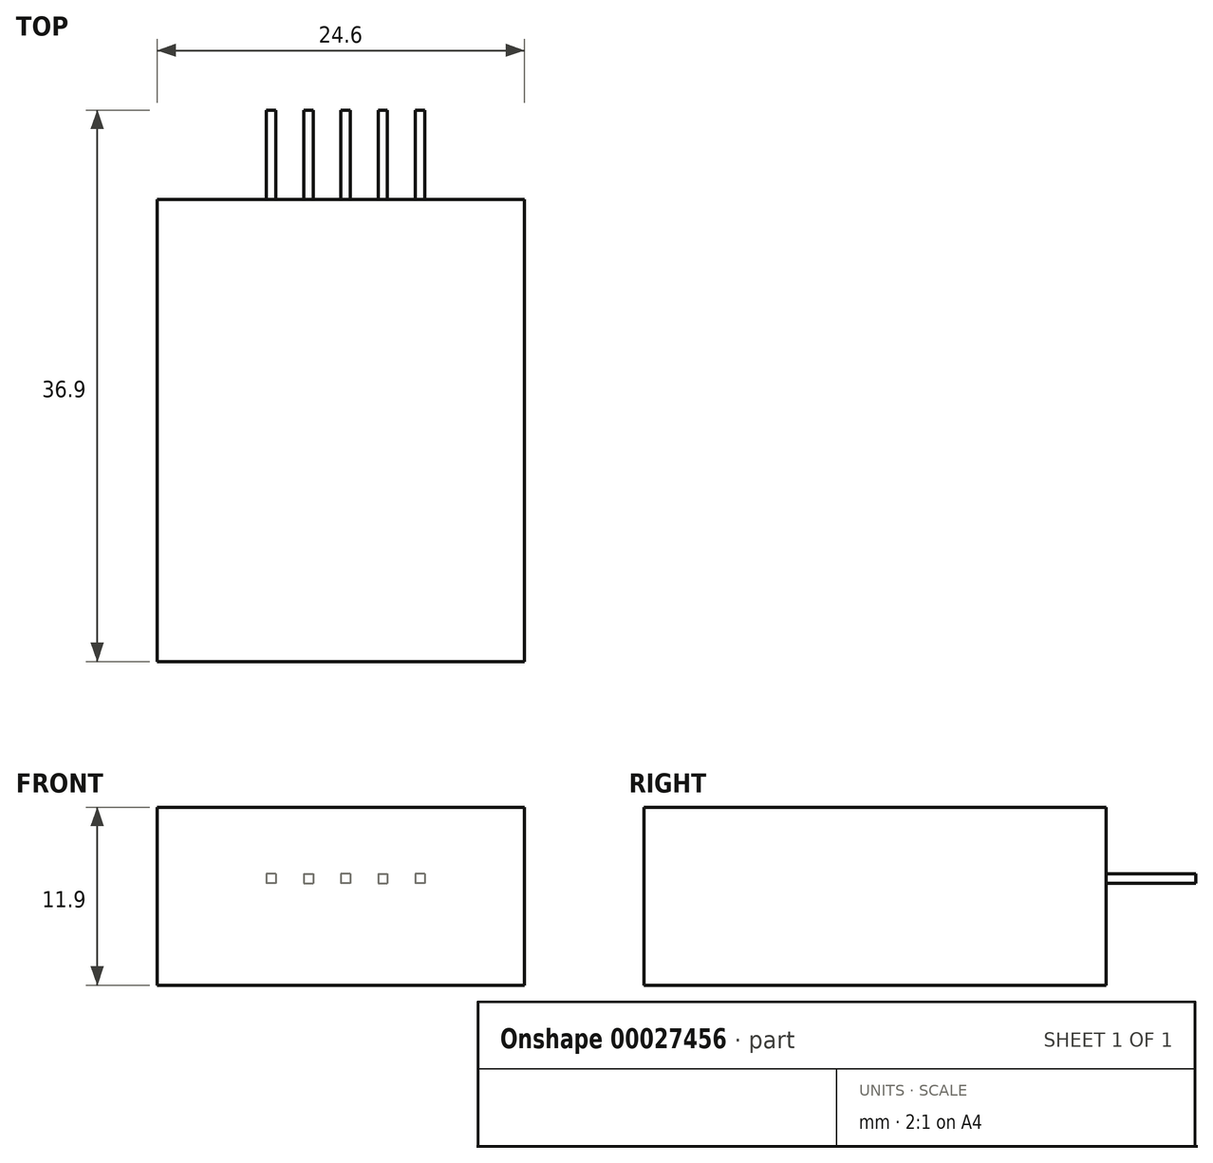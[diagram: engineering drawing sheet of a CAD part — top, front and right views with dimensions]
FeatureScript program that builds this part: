
annotation { "Feature Type Name" : "Feature", "Feature Type Description" : "" }
export const myFeature = defineFeature(function(context is Context, id is Id, definition is map)
    precondition{}
    {
        {
            var Q0;
            Q0=qCreatedBy(makeId("Top.planeOp"),FACE);
            var sketch = newSketch(context, id + "F0", { "sketchPlane" : qUnion([Q0])});
            skLineSegment(sketch, "E0.rect.bottom", {"start": v(12.3, 15.45) * mm, "end": v(-12.3, 15.45) * mm});
            skLineSegment(sketch, "E0.rect.top", {"start": v(12.3, -15.45) * mm, "end": v(-12.3, -15.45) * mm});
            skLineSegment(sketch, "E0.rect.left", {"start": v(12.3, 15.45) * mm, "end": v(12.3, -15.45) * mm});
            skLineSegment(sketch, "E0.rect.right", {"start": v(-12.3, 15.45) * mm, "end": v(-12.3, -15.45) * mm});
            skPoint(sketch, "E0.rect.middle", {"position": v(0, 0) * mm});
            skSolve(sketch);
        }
        {
            var Q0;
            Q0=makeQuery(id+"F0.imprint","IMPRINT",FACE,{"disambiguationData":[TD([[makeQuery(id+"F0.imprint","IMPRINT",EDGE,{"derivedFrom":sQuery(id+"F0.wireOp",EDGE,"E0.rect.bottom")}),1.0]])]});
            extrude(context, id + "F1", {"entities" : qUnion([Q0]), "depth" : 11.9 * mm});
        }
        {
            var Q0;
            Q0=makeQuery(id+"F1.opExtrude","SWEPT_FACE",FACE,{"disambiguationData":[OSD([sQuery(id+"F0.wireOp",EDGE,"E0.rect.bottom")])]});
            var sketch = newSketch(context, id + "F2", { "sketchPlane" : qUnion([Q0])});
            skLineSegment(sketch, "E1.bottom", {"start": v(-6.55, 8.44) * mm, "end": v(5.9, 8.44) * mm});
            skLineSegment(sketch, "E1.top", {"start": v(-6.55, 5.84) * mm, "end": v(5.9, 5.84) * mm});
            skLineSegment(sketch, "E1.left", {"start": v(-6.55, 8.44) * mm, "end": v(-6.55, 5.84) * mm});
            skLineSegment(sketch, "E1.right", {"start": v(5.9, 8.44) * mm, "end": v(5.9, 5.84) * mm});
            skLineSegment(sketch, "E2", {"start": v(-4.06, 8.44) * mm, "end": v(-4.06, 5.84) * mm});
            skLineSegment(sketch, "E3", {"start": v(-1.57, 8.44) * mm, "end": v(-1.57, 5.84) * mm});
            skLineSegment(sketch, "E4", {"start": v(0.92, 8.44) * mm, "end": v(0.92, 5.84) * mm});
            skLineSegment(sketch, "E5", {"start": v(3.4, 8.44) * mm, "end": v(3.4, 5.84) * mm});
            skLineSegment(sketch, "E6.bottom", {"start": v(-5.62, 7.45) * mm, "end": v(-5, 7.45) * mm});
            skLineSegment(sketch, "E6.top", {"start": v(-5.62, 6.82) * mm, "end": v(-5, 6.82) * mm});
            skLineSegment(sketch, "E6.left", {"start": v(-5.62, 7.45) * mm, "end": v(-5.62, 6.82) * mm});
            skLineSegment(sketch, "E6.right", {"start": v(-5, 7.46) * mm, "end": v(-5, 6.82) * mm});
            skLineSegment(sketch, "E7", {"start": v(-5.3, 8.44) * mm, "end": v(-5.3, 7.45) * mm, "construction": true});
            skLineSegment(sketch, "E8", {"start": v(-5, 7.14) * mm, "end": v(-4.06, 7.14) * mm, "construction": true});
            skLineSegment(sketch, "E9", {"start": v(-5.3, 6.82) * mm, "end": v(-5.3, 5.84) * mm, "construction": true});
            skLineSegment(sketch, "E10", {"start": v(-6.55, 7.14) * mm, "end": v(-5.62, 7.14) * mm, "construction": true});
            skLineSegment(sketch, "E11.MirrorCS", {"start": v(-3.13, 7.46) * mm, "end": v(-3.13, 6.82) * mm});
            skLineSegment(sketch, "E12.MirrorCS", {"start": v(-2.5, 7.45) * mm, "end": v(-3.13, 7.45) * mm});
            skLineSegment(sketch, "E13.MirrorCS", {"start": v(-2.5, 7.45) * mm, "end": v(-2.5, 6.82) * mm});
            skLineSegment(sketch, "E14.MirrorCS", {"start": v(-2.5, 6.82) * mm, "end": v(-3.13, 6.82) * mm});
            skLineSegment(sketch, "E15.MirrorCS", {"start": v(-0.64, 7.46) * mm, "end": v(-0.01, 7.46) * mm});
            skLineSegment(sketch, "E16.MirrorCS", {"start": v(-0.64, 7.46) * mm, "end": v(-0.64, 6.82) * mm});
            skLineSegment(sketch, "E17.MirrorCS", {"start": v(-0.01, 7.46) * mm, "end": v(-0.01, 6.82) * mm});
            skLineSegment(sketch, "E18.MirrorCS", {"start": v(-0.64, 6.82) * mm, "end": v(-0.01, 6.82) * mm});
            skLineSegment(sketch, "E19.MirrorCS", {"start": v(1.85, 7.46) * mm, "end": v(1.85, 6.82) * mm});
            skLineSegment(sketch, "E20.MirrorCS", {"start": v(2.48, 7.46) * mm, "end": v(1.85, 7.46) * mm});
            skLineSegment(sketch, "E21.MirrorCS", {"start": v(2.48, 7.46) * mm, "end": v(2.48, 6.82) * mm});
            skLineSegment(sketch, "E22.MirrorCS", {"start": v(2.48, 6.82) * mm, "end": v(1.85, 6.82) * mm});
            skLineSegment(sketch, "E23.MirrorCS", {"start": v(4.34, 7.46) * mm, "end": v(4.97, 7.46) * mm});
            skLineSegment(sketch, "E24.MirrorCS", {"start": v(4.34, 7.46) * mm, "end": v(4.34, 6.82) * mm});
            skLineSegment(sketch, "E25.MirrorCS", {"start": v(4.97, 7.46) * mm, "end": v(4.97, 6.82) * mm});
            skLineSegment(sketch, "E26.MirrorCS", {"start": v(4.34, 6.82) * mm, "end": v(4.97, 6.82) * mm});
            skSolve(sketch);
        }
        {
            var Q0;
            Q0=makeQuery(id+"F2.imprint","IMPRINT",FACE,{"disambiguationData":[TD([[makeQuery(id+"F2.imprint","IMPRINT",EDGE,{"derivedFrom":sQuery(id+"F2.wireOp",EDGE,"E6.bottom")}),-1.0]])]});
            var Q1;
            Q1=makeQuery(id+"F2.imprint","IMPRINT",FACE,{"disambiguationData":[TD([[makeQuery(id+"F2.imprint","IMPRINT",EDGE,{"derivedFrom":sQuery(id+"F2.wireOp",EDGE,"E11.MirrorCS")}),1.0]])]});
            var Q2;
            Q2=makeQuery(id+"F2.imprint","IMPRINT",FACE,{"disambiguationData":[TD([[makeQuery(id+"F2.imprint","IMPRINT",EDGE,{"derivedFrom":sQuery(id+"F2.wireOp",EDGE,"E19.MirrorCS")}),1.0]])]});
            var Q3;
            Q3=makeQuery(id+"F2.imprint","IMPRINT",FACE,{"disambiguationData":[TD([[makeQuery(id+"F2.imprint","IMPRINT",EDGE,{"derivedFrom":sQuery(id+"F2.wireOp",EDGE,"E23.MirrorCS")}),-1.0]])]});
            var Q4;
            Q4=makeQuery(id+"F2.imprint","IMPRINT",FACE,{"disambiguationData":[TD([[makeQuery(id+"F2.imprint","IMPRINT",EDGE,{"derivedFrom":sQuery(id+"F2.wireOp",EDGE,"E15.MirrorCS")}),-1.0]])]});
            extrude(context, id + "F3", {"entities" : qUnion([Q0, Q1, Q2, Q3, Q4]), "operationType" : NewBodyOperationType.ADD, "depth" : 6 * mm});
        }
    });
